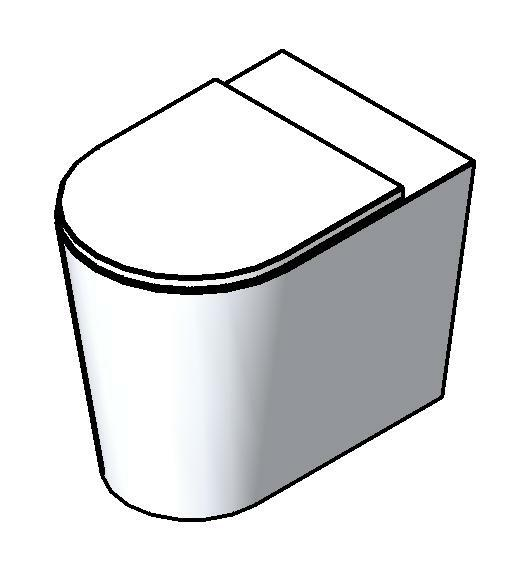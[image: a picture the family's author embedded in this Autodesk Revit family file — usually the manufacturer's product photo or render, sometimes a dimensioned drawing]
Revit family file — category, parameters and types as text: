
# Revit family: Deca_Bacia Sanitária Convencional Link_P.23
name_source: partatom
category: Plumbing Fixtures
revit_build: Autodesk Revit Architecture 2012 (Build: 20110916_2132(x64)
units: mm (PartAtom-declared; Revit-internal decimal feet)

## types (2) — shared parameters
Aprovado por = Contino/quattroD
Assembly Code = D2010100
Atendimento ao Cliente = 0800-011-7073
Consumo = 6lpf
Criado por = Contino/quattroD
Description = Bacia sanitária convencional
Diâmetro Ponto de Esgoto = 100 mm  [stored 0.328084 ft]
Diâmetro Água Fria = 40 mm  [stored 0.131234 ft]
Flow Pressure = 0.00 psi
Linha = LK
Louça/Metais = Louça
Manufacturer = Deca
Material = Deca_Vitreous China
Norma = ABNT NBR 15097-1: 2011 / ABNT NBR 15097-2: 2011
Peso Liquido (Kg) = 32
Pressão = 2 a 40 mca
Produto = Bacia sanitária convencional LK
Raio Ponto de Esgoto = 50 mm  [stored 0.164042 ft]
Raio Água Fria = 20 mm  [stored 0.0656168 ft]
Segmento = Luxo
URL = www.deca.com.br/produtos
Variações de COR = Branco (P.23.17); Ébano (P.23.95).
Vendido Separadamente = Anel de vedação: (AV.90.01 ).Tubo de ligação com anel expansor: Cromado (1968.C), Branco (1968.E.BR), Dourado (1968.D).Parafuso de fixação: Cromado (SP.13.01) e Dourado (SP.130.03).Assentos Compatíveis:Assento Poliéster com fixação cromada: Branco (AP.23.17), Ébano (AP.23.95);Assento Poliéster com fixação dourada: Branco (AP.230.17), Ébano (AP.230.95);Assento termofixo Slowclose e Easy Clen: Branco (AP.236.17), Ébano (AP.236.95);Assento Poliéster Slow Close: Branco (AP.237.17).
zero-valued in all types: CWFU, Default Elevation, WFU

## per-type parameters (varying)
| type | Bacia | Código | Model |
| P.23_Branco Gelo GE17 | Deca GE17 Branco Gelo Cerâmica | P.23.17 | P.23.17 |
| P.23_Ébano EB95 | Deca EB95 Ébano Cerâmica | P.23.95 | P.23.95 |

note: [stored X ft] marks values corroborated as IEEE doubles in the binary element streams (Revit-internal decimal feet)

## geometry (parser evidence)
native form markers: Blend x20, Sweep x5
no freeform markers — native parametric forms only
